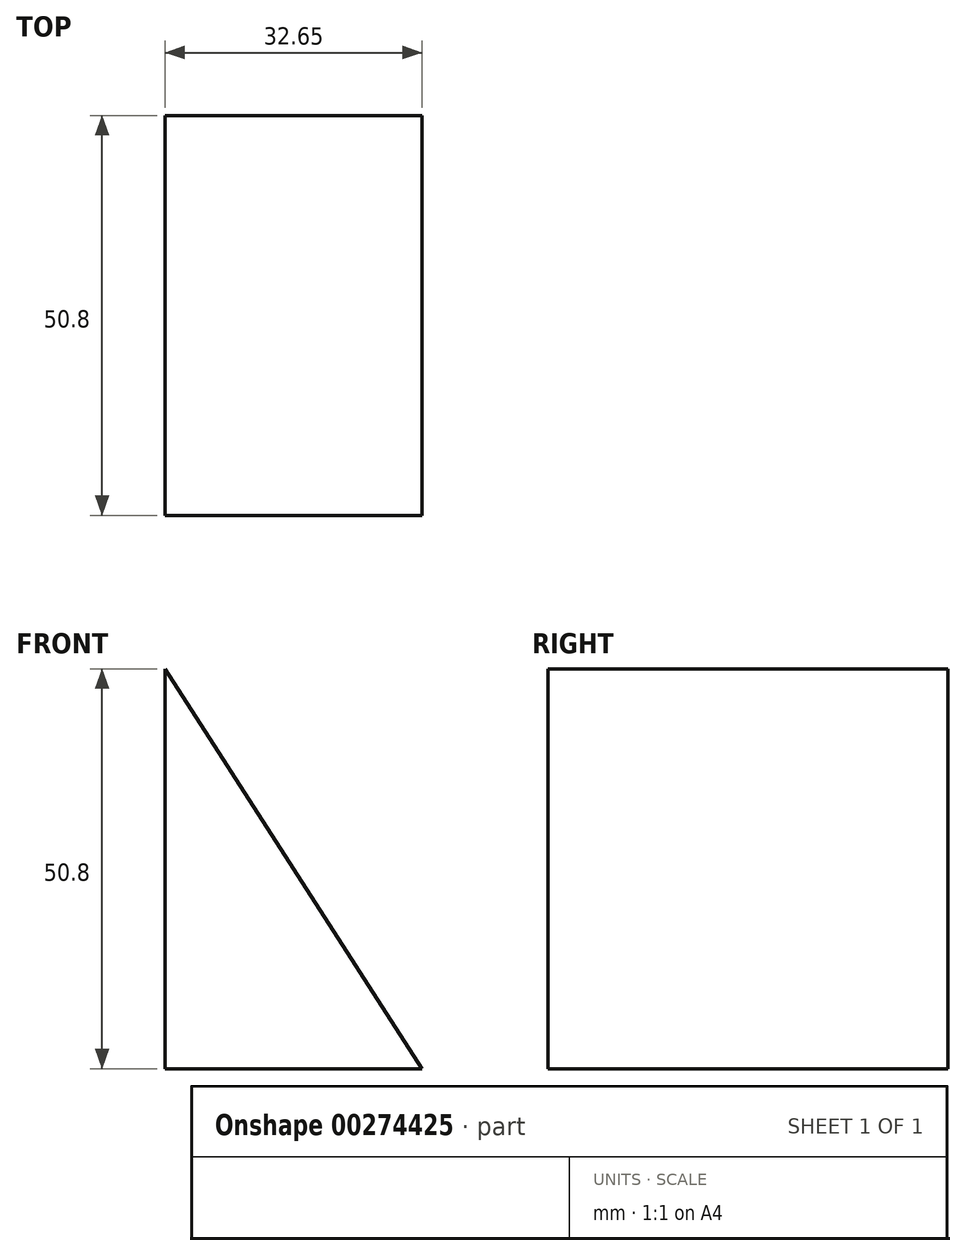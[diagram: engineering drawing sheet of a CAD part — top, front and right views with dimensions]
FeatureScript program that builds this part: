
annotation { "Feature Type Name" : "Feature", "Feature Type Description" : "" }
export const myFeature = defineFeature(function(context is Context, id is Id, definition is map)
    precondition{}
    {
        {
            var Q0;
            Q0=qCreatedBy(makeId("Front.planeOp"),FACE);
            var sketch = newSketch(context, id + "F0", { "sketchPlane" : qUnion([Q0])});
            skLineSegment(sketch, "E0", {"start": v(-76.2, 50.8) * mm, "end": v(-43.54, 0) * mm});
            skLineSegment(sketch, "E1", {"start": v(-43.54, 0) * mm, "end": v(-76.2, 0) * mm});
            skLineSegment(sketch, "E2", {"start": v(-76.2, 50.8) * mm, "end": v(-76.2, 0) * mm});
            skSolve(sketch);
        }
        {
            var Q0;
            Q0=makeQuery(id+"F0.imprint","IMPRINT",FACE,{"disambiguationData":[TD([[makeQuery(id+"F0.imprint","IMPRINT",EDGE,{"derivedFrom":sQuery(id+"F0.wireOp",EDGE,"E0")}),-1.0]])]});
            extrude(context, id + "F1", {"entities" : qUnion([Q0]), "depth" : 50.8 * mm});
        }
    });
